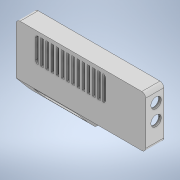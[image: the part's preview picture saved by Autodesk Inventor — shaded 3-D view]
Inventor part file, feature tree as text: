
AUTODESK INVENTOR PART (.ipt)
format: ipt  version: 2021 (Build 250183000, 183)  size: 547,840 bytes
history: native  units: mm
features: sketch x22, extrude x21, chamfer x6, fillet x4, hole x1
ambient origin geometry x8: Origin, YZ Plane, XZ Plane, XY Plane, X Axis, Y Axis, Z Axis, Center Point
bodies: Solid1 (feature_tree)
feature tree (54):
  extrude  "Extrusion1"  Depth=100.0mm
  extrude  "Extrusion3"  Depth=50.0mm
  extrude  "Extrusion4"  Depth=12.5mm
  extrude  "Extrusion12"  Depth=3.0mm TaperAngle=0.0deg
  extrude  "Extrusion13"  Depth=3.0mm TaperAngle=0.0deg
  fillet  "Fillet3"  Radius=2.0mm
  extrude  "Extrusion15"  Depth=2.0mm
  extrude  "Extrusion20"  Depth=1.2mm
  extrude  "Extrusion21"  Depth=12.0mm TaperAngle=0.0deg
  extrude  "Extrusion22"  Depth=2.0mm
  extrude  "Extrusion23"  Depth=3.0mm
  extrude  "Extrusion26"  Depth=4.4mm TaperAngle=0.0deg
  hole  "Hole2"  [1 undecoded]
  chamfer  "Chamfer3"  Distance=12.0mm
  chamfer  "Chamfer4"  Distance=12.0mm
  chamfer  "Chamfer5"  Distance=2.0mm
  chamfer  "Chamfer6"  Distance=2.0mm
  chamfer  "Chamfer7"  Distance=3.0mm
  extrude  "Extrusion27"  Depth=3.0mm
  fillet  "Fillet4"  Radius=3.0mm
  extrude  "Extrusion28"  Depth=50.0mm
  extrude  "Extrusion29"  Depth=0.5mm
  extrude  "Extrusion30"  Depth=15.0mm
  fillet  "Fillet5"  Radius=3.0mm
  extrude  "Extrusion34"  Depth=3.0mm
  extrude  "Extrusion35"  Depth=0.5mm
  extrude  "Extrusion36"  Depth=0.5mm
  extrude  "Extrusion37"  Depth=0.5mm
  fillet  "Fillet6"  Radius=4.8mm
  extrude  "Extrusion38"  Depth=0.5mm
  extrude  "Extrusion39"  Depth=0.5mm
  chamfer  "Chamfer8"  Distance=4.8mm
  sketch  "Sketch1"  dims[d0=52.0mm d1=100.0mm]
  sketch  "Sketch4"  dims[d2=26.0mm d3=50.0mm]
  sketch  "Sketch5"  dims[d4=2.0mm d5=0.0mm d35=12.5mm]
  sketch  "Sketch13"  dims[d36=63.1mm d37=3.0mm d38=0.0mm]
  sketch  "Sketch14"  dims[d39=50.673mm d40=3.0mm d41=0.0mm d79=2.0mm]
  sketch  "Sketch16"  dims[d80=2.0mm d81=2.0mm]
  sketch  "Sketch21"  dims[d82=1.2mm d83=44.0mm]
  sketch  "Sketch22"  dims[d84=59.0mm d85=12.0mm d86=0.0mm]
  sketch  "Sketch23"  dims[d87=2.0mm d88=12.6mm]
  sketch  "Sketch24"  dims[d89=12.0mm d90=0.0mm d91=3.0mm]
  sketch  "Sketch27"  dims[d95=33.8mm d96=4.4mm d97=0.0mm]
  sketch  "Sketch28"  dims[d117=2.0mm d118=2.0mm d119=12.0mm d120=0.0mm d121=12.0mm d122=0.0mm]
  sketch  "Sketch29"  dims[d123=70.0mm]
  sketch  "Sketch30"  dims[d124=89.0mm]
  sketch  "Sketch31"  dims[d125=8.0mm]
  sketch  "Sketch32"  dims[d126=8.0mm d127=2.0mm d128=0.0mm]
  sketch  "Sketch36"  dims[d129=8.0mm]
  sketch  "Sketch37"  dims[d130=10.0mm]
  sketch  "Sketch38"  dims[d131=12.0mm]
  sketch  "Sketch39"  dims[d132=8.0mm]
  sketch  "Sketch40"  dims[d133=8.0mm]
  sketch  "Sketch41"  dims[d134=8.0mm d135=2.0mm d136=0.0mm d144=3.0mm d145=3.0mm d146=3.0mm d147=50.0mm d148=97.0mm d149=15.0mm d150=3.0mm d151=3.0mm d152=97.0mm d153=49.0mm d154=4.8mm d155=4.8mm d156=4.8mm d157=4.8mm d158=4.8mm d159=5.0mm d160=0.0mm d161=2.0mm d162=6.0mm d163=4.0mm d164=2.0mm d165=90.0deg d166=4.0mm d167=20.594885mm d168=2.0mm d169=2.0mm d170=45.0deg d171=1.0mm d172=2.0mm d173=45.0deg d174=2.0mm d175=2.0mm d176=45.0deg d177=2.0mm d178=2.0mm d179=45.0deg d180=0.8mm d181=2.0mm d182=45.0deg d184=68.0mm d189=2.0mm d190=0.0mm d191=2.0mm d192=2.0mm d193=24.0mm d194=2.0mm d195=0.0mm d196=36.5mm d197=46.5mm d198=3.5mm d199=2.0mm d200=0.0mm d201=12.5mm d202=23.0mm d203=3.5mm d204=2.0mm d205=0.0mm d206=1.0mm d217=7.6mm d218=10.0mm d219=46.4mm d220=20.0mm d221=0.0mm d222=22.68928mm d223=67.0mm d224=0.0mm d225=1.2mm d226=0.0mm d227=1.2mm d228=0.0mm d229=3.0mm d230=12.3mm d231=33.2mm d232=1.0mm d233=10.0mm d234=1.2mm d235=0.0mm d236=1.2mm d237=5.0mm d238=20.0mm d239=2.0mm d240=0.0mm d241=2.0mm d242=2.0mm d243=45.0deg d67=0.5mm d68=0.872665mm d69=0.5mm d70=0.872665mm d71=0.5mm d72=0.872665mm d73=0.5mm d74=0.872665mm d75=0.872665mm d76=0.5mm d77=0.872665mm d208=0.5mm d209=0.872665mm d210=0.5mm d211=0.872665mm]
note: 1 required parameter value undecoded (feature->parameter linkage not recoverable at this tier; creation-order binding heuristic only, values carry confidence <= 0.55)
